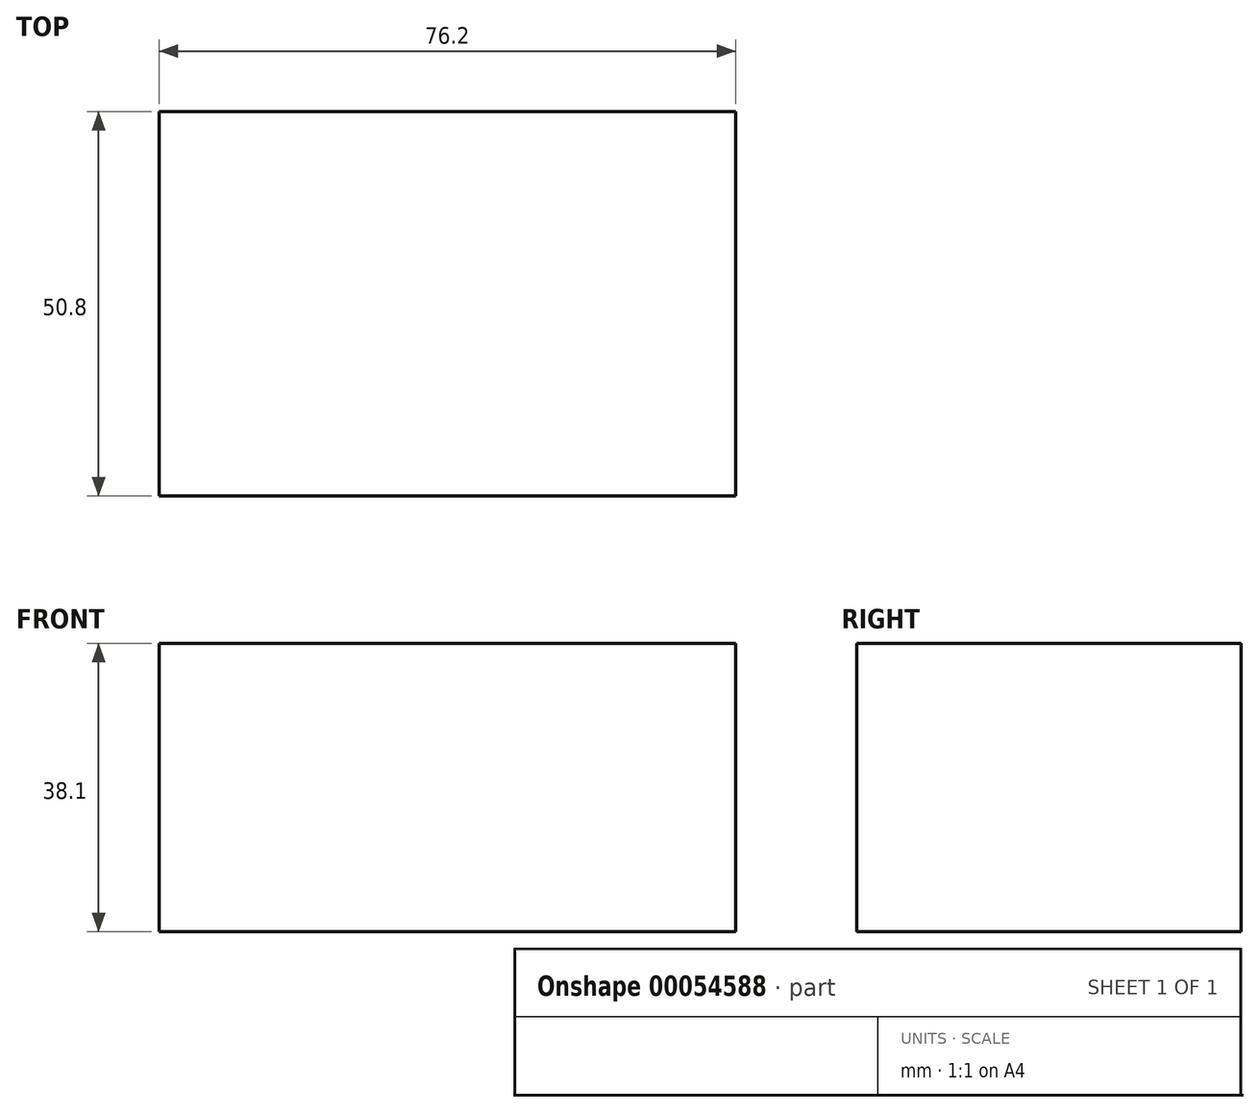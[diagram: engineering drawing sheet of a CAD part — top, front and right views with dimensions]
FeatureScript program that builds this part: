
annotation { "Feature Type Name" : "Feature", "Feature Type Description" : "" }
export const myFeature = defineFeature(function(context is Context, id is Id, definition is map)
    precondition{}
    {
        {
            var Q0;
            Q0=qCreatedBy(makeId("Top.planeOp"),FACE);
            var sketch = newSketch(context, id + "F0", { "sketchPlane" : qUnion([Q0])});
            skLineSegment(sketch, "E0.rect.bottom", {"start": v(38.1, 25.4) * mm, "end": v(-38.1, 25.4) * mm});
            skLineSegment(sketch, "E0.rect.top", {"start": v(38.1, -25.4) * mm, "end": v(-38.1, -25.4) * mm});
            skLineSegment(sketch, "E0.rect.left", {"start": v(38.1, 25.4) * mm, "end": v(38.1, -25.4) * mm});
            skLineSegment(sketch, "E0.rect.right", {"start": v(-38.1, 25.4) * mm, "end": v(-38.1, -25.4) * mm});
            skPoint(sketch, "E0.rect.middle", {"position": v(0, 0) * mm});
            skSolve(sketch);
        }
        {
            var Q0;
            Q0 = qSketchRegion(id + "F0", true);
            extrude(context, id + "F1", {"entities" : qUnion([Q0]), "depth" : 38.1 * mm});
        }
    });
